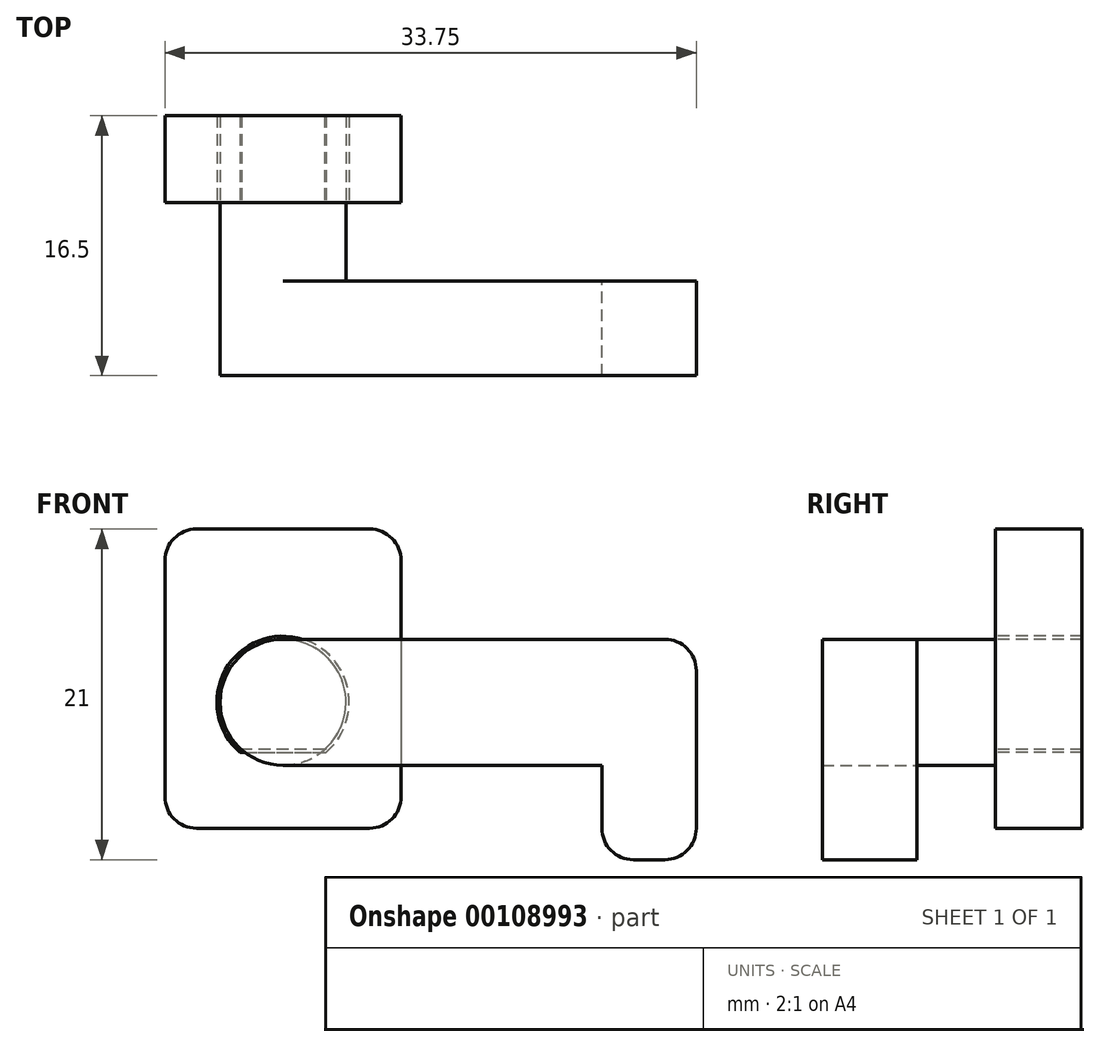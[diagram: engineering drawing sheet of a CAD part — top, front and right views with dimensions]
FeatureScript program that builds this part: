
annotation { "Feature Type Name" : "Feature", "Feature Type Description" : "" }
export const myFeature = defineFeature(function(context is Context, id is Id, definition is map)
    precondition{}
    {
        {
            var Q0;
            Q0=qCreatedBy(makeId("Front.planeOp"),FACE);
            var sketch = newSketch(context, id + "F0", { "sketchPlane" : qUnion([Q0])});
            skCircle(sketch, "E0", {"center": v(0, 0) * mm, "radius": 4 * mm});
            skLineSegment(sketch, "E1", {"start": v(-7.5, 11) * mm, "end": v(-7.5, -8) * mm});
            skLineSegment(sketch, "E2", {"start": v(-7.5, 11) * mm, "end": v(0, 11) * mm});
            skLineSegment(sketch, "E3", {"start": v(-7.5, -8) * mm, "end": v(0, -8) * mm});
            skLineSegment(sketch, "E4.MirrorCS", {"start": v(7.5, 11) * mm, "end": v(0, 11) * mm});
            skLineSegment(sketch, "E5.MirrorCS", {"start": v(7.5, 11) * mm, "end": v(7.5, -8) * mm});
            skLineSegment(sketch, "E6.MirrorCS", {"start": v(7.5, -8) * mm, "end": v(0, -8) * mm});
            skLineSegment(sketch, "E7", {"start": v(-7.5, -3) * mm, "end": v(7.5, -3) * mm});
            skCircle(sketch, "E8.0", {"center": v(0, 0) * mm, "radius": 4.2 * mm});
            skLineSegment(sketch, "E9.0", {"start": v(-7.5, -3.2) * mm, "end": v(7.5, -3.2) * mm});
            skSolve(sketch);
        }
        {
            var Q0;
            {var subQ1=sQuery(id+"F0.wireOp",EDGE,"E3");Q0=makeQuery(id+"F0.imprint","IMPRINT",FACE,{"disambiguationData":[TD([[makeQuery(id+"F0.imprint","IMPRINT",EDGE,{"derivedFrom":subQ1}),1.0]])]});}
            var Q1;
            {var subQ0=sQuery(id+"F0.wireOp",EDGE,"E9.0");var subQ1=sQuery(id+"F0.wireOp",EDGE,"E0");var subQ2=makeQuery(id+"F0.imprint","INTERSECT",VERTEX,{"disambiguationData":[OD(0.0)],"derivedFrom":[subQ1,subQ0]});Q1=makeQuery(id+"F0.imprint","IMPRINT",FACE,{"disambiguationData":[TD([[makeQuery(id+"F0.imprint","IMPRINT",EDGE,{"disambiguationData":[TD([[subQ2,-1.0]])],"derivedFrom":subQ1}),-1.0]])]});}
            var Q2;
            {var subQ0=sQuery(id+"F0.wireOp",EDGE,"E9.0");var subQ1=sQuery(id+"F0.wireOp",EDGE,"E0");var subQ2=makeQuery(id+"F0.imprint","INTERSECT",VERTEX,{"disambiguationData":[OD(0.0)],"derivedFrom":[subQ1,subQ0]});Q2=makeQuery(id+"F0.imprint","IMPRINT",FACE,{"disambiguationData":[TD([[makeQuery(id+"F0.imprint","IMPRINT",EDGE,{"disambiguationData":[TD([[subQ2,-1.0]])],"derivedFrom":subQ1}),1.0]])]});}
            var Q3;
            {var subQ0=sQuery(id+"F0.wireOp",EDGE,"E7");var subQ1=sQuery(id+"F0.wireOp",EDGE,"E5.MirrorCS");var subQ2=makeQuery(id+"F0.imprint","INTERSECT",VERTEX,{"derivedFrom":[subQ1,subQ0]});Q3=makeQuery(id+"F0.imprint","IMPRINT",FACE,{"disambiguationData":[TD([[makeQuery(id+"F0.imprint","IMPRINT",EDGE,{"disambiguationData":[TD([[subQ2,-1.0]])],"derivedFrom":subQ1}),-1.0]])]});}
            var Q4;
            {var subQ0=sQuery(id+"F0.wireOp",EDGE,"E7");var subQ1=sQuery(id+"F0.wireOp",EDGE,"E1");var subQ2=makeQuery(id+"F0.imprint","INTERSECT",VERTEX,{"derivedFrom":[subQ1,subQ0]});Q4=makeQuery(id+"F0.imprint","IMPRINT",FACE,{"disambiguationData":[TD([[makeQuery(id+"F0.imprint","IMPRINT",EDGE,{"disambiguationData":[TD([[subQ2,-1.0]])],"derivedFrom":subQ1}),1.0]])]});}
            var Q5;
            {var subQ7=sQuery(id+"F0.wireOp",EDGE,"E2");Q5=makeQuery(id+"F0.imprint","IMPRINT",FACE,{"disambiguationData":[TD([[makeQuery(id+"F0.imprint","IMPRINT",EDGE,{"derivedFrom":subQ7}),-1.0]])]});}
            extrude(context, id + "F1", {"entities" : qUnion([Q0, Q1, Q2, Q3, Q4, Q5]), "oppositeDirection" : true, "depth" : 5.5 * mm});
        }
        {
            var Q0;
            Q0=makeQuery(id+"F1.opExtrude","SWEPT_EDGE",EDGE,{"disambiguationData":[OSD([sQuery(id+"F0.wireOp",EDGE,"E1"),sQuery(id+"F0.wireOp",EDGE,"E3")])]});
            var Q1;
            Q1=makeQuery(id+"F1.opExtrude","SWEPT_EDGE",EDGE,{"disambiguationData":[OSD([sQuery(id+"F0.wireOp",EDGE,"E5.MirrorCS"),sQuery(id+"F0.wireOp",EDGE,"E6.MirrorCS")])]});
            var Q2;
            Q2=makeQuery(id+"F1.opExtrude","SWEPT_EDGE",EDGE,{"disambiguationData":[OSD([sQuery(id+"F0.wireOp",EDGE,"E1"),sQuery(id+"F0.wireOp",EDGE,"E2")])]});
            var Q3;
            Q3=makeQuery(id+"F1.opExtrude","SWEPT_EDGE",EDGE,{"disambiguationData":[OSD([sQuery(id+"F0.wireOp",EDGE,"E4.MirrorCS"),sQuery(id+"F0.wireOp",EDGE,"E5.MirrorCS")])]});
            fillet(context, id + "F2", {"entities" : qUnion([Q0, Q1, Q2, Q3]), "radius" : 2 * mm, "tangentPropagation" : true, "allowEdgeOverflow" : false});
        }
        {
            var Q0;
            {var subQ0=sQuery(id+"F0.wireOp",EDGE,"E7");var subQ1=sQuery(id+"F0.wireOp",EDGE,"E0");var subQ2=makeQuery(id+"F0.imprint","INTERSECT",VERTEX,{"disambiguationData":[OD(0.0)],"derivedFrom":[subQ1,subQ0]});Q0=makeQuery(id+"F0.imprint","IMPRINT",FACE,{"disambiguationData":[TD([[makeQuery(id+"F0.imprint","IMPRINT",EDGE,{"disambiguationData":[TD([[subQ2,1.0]])],"derivedFrom":subQ1}),1.0]])]});}
            var Q1;
            Q1=makeQuery(id+"F1.opExtrude","CAP_FACE",FACE,{"disambiguationData":[OSD([sQuery(id+"F0.wireOp",EDGE,"E0"),sQuery(id+"F0.wireOp",EDGE,"E1"),sQuery(id+"F0.wireOp",EDGE,"E2"),sQuery(id+"F0.wireOp",EDGE,"E3"),sQuery(id+"F0.wireOp",EDGE,"E4.MirrorCS"),sQuery(id+"F0.wireOp",EDGE,"E5.MirrorCS"),sQuery(id+"F0.wireOp",EDGE,"E6.MirrorCS")])],"isStart":false});
            extrude(context, id + "F3", {"entities" : qUnion([Q0]), "endBound" : BoundingType.UP_TO_SURFACE, "oppositeDirection" : true, "endBoundEntityFace" : qUnion([Q1]), "depth" : 25 * mm});
        }
        {
            var Q0;
            {var subQ0=sQuery(id+"F0.wireOp",EDGE,"E7");var subQ1=sQuery(id+"F0.wireOp",EDGE,"E0");var subQ2=makeQuery(id+"F0.imprint","INTERSECT",VERTEX,{"disambiguationData":[OD(0.0)],"derivedFrom":[subQ1,subQ0]});Q0=makeQuery(id+"F0.imprint","IMPRINT",FACE,{"disambiguationData":[TD([[makeQuery(id+"F0.imprint","IMPRINT",EDGE,{"disambiguationData":[TD([[subQ2,1.0]])],"derivedFrom":subQ1}),1.0]])]});}
            var Q1;
            {var subQ0=sQuery(id+"F0.wireOp",EDGE,"E9.0");var subQ1=sQuery(id+"F0.wireOp",EDGE,"E0");var subQ2=makeQuery(id+"F0.imprint","INTERSECT",VERTEX,{"disambiguationData":[OD(0.0)],"derivedFrom":[subQ1,subQ0]});Q1=makeQuery(id+"F0.imprint","IMPRINT",FACE,{"disambiguationData":[TD([[makeQuery(id+"F0.imprint","IMPRINT",EDGE,{"disambiguationData":[TD([[subQ2,1.0]])],"derivedFrom":subQ1}),1.0]])]});}
            var Q2;
            {var subQ0=sQuery(id+"F0.wireOp",EDGE,"E9.0");var subQ1=sQuery(id+"F0.wireOp",EDGE,"E0");var subQ2=makeQuery(id+"F0.imprint","INTERSECT",VERTEX,{"disambiguationData":[OD(0.0)],"derivedFrom":[subQ1,subQ0]});Q2=makeQuery(id+"F0.imprint","IMPRINT",FACE,{"disambiguationData":[TD([[makeQuery(id+"F0.imprint","IMPRINT",EDGE,{"disambiguationData":[TD([[subQ2,-1.0]])],"derivedFrom":subQ1}),1.0]])]});}
            extrude(context, id + "F4", {"entities" : qUnion([Q0, Q1, Q2]), "operationType" : NewBodyOperationType.ADD, "depth" : 5 * mm});
        }
        {
            var Q0;
            Q0=makeQuery(id+"F4.opExtrude","CAP_FACE",FACE,{"disambiguationData":[OSD([sQuery(id+"F0.wireOp",EDGE,"E0")])],"isStart":false});
            var sketch = newSketch(context, id + "F5", { "sketchPlane" : qUnion([Q0])});
            skLineSegment(sketch, "E10", {"start": v(0, 4) * mm, "end": v(18.25, 4) * mm});
            skLineSegment(sketch, "E11", {"start": v(0, -4) * mm, "end": v(18.25, -4) * mm});
            skArc(sketch, "E12", {"start": v(0, 4) * mm, "mid": v(-4, 0) * mm, "end": v(0, -4) * mm});
            skLineSegment(sketch, "E13", {"start": v(18.25, 10.29) * mm, "end": v(18.25, -14.12) * mm, "construction": true});
            skLineSegment(sketch, "E14", {"start": v(-5.71, -10) * mm, "end": v(30.22, -10) * mm, "construction": true});
            skLineSegment(sketch, "E15", {"start": v(20.25, 4) * mm, "end": v(26.25, 4) * mm});
            skLineSegment(sketch, "E16", {"start": v(26.25, 4) * mm, "end": v(26.25, -10) * mm});
            skLineSegment(sketch, "E17", {"start": v(26.25, -10) * mm, "end": v(20.25, -10) * mm});
            skLineSegment(sketch, "E18", {"start": v(20.25, -10) * mm, "end": v(20.25, -4) * mm});
            skLineSegment(sketch, "E19", {"start": v(20.25, -4) * mm, "end": v(18.25, -4) * mm});
            skLineSegment(sketch, "E20", {"start": v(20.25, 4) * mm, "end": v(18.25, 4) * mm});
            skSolve(sketch);
        }
        {
            var Q0;
            {var subQ1=sQuery(id+"F5.wireOp",EDGE,"E10");Q0=makeQuery(id+"F5.imprint","IMPRINT",FACE,{"disambiguationData":[TD([[makeQuery(id+"F5.imprint","IMPRINT",EDGE,{"derivedFrom":subQ1}),-1.0]])]});}
            var Q1;
            {var subQ0=sQuery(id+"F5.wireOp",EDGE,"E12");Q1=makeQuery(id+"F5.imprint","IMPRINT",FACE,{"disambiguationData":[TD([[makeQuery(id+"F5.imprint","IMPRINT",EDGE,{"derivedFrom":subQ0}),1.0]])]});}
            extrude(context, id + "F6", {"entities" : qUnion([Q0, Q1]), "operationType" : NewBodyOperationType.ADD, "depth" : 6 * mm});
        }
        {
            var Q0;
            Q0=makeQuery(id+"F6.opExtrude","SWEPT_EDGE",EDGE,{"disambiguationData":[OSD([sQuery(id+"F5.wireOp",EDGE,"E15"),sQuery(id+"F5.wireOp",EDGE,"E16")])]});
            var Q1;
            Q1=makeQuery(id+"F6.opExtrude","SWEPT_EDGE",EDGE,{"disambiguationData":[OSD([sQuery(id+"F5.wireOp",EDGE,"E16"),sQuery(id+"F5.wireOp",EDGE,"E17")])]});
            var Q2;
            Q2=makeQuery(id+"F6.opExtrude","SWEPT_EDGE",EDGE,{"disambiguationData":[OSD([sQuery(id+"F5.wireOp",EDGE,"E17"),sQuery(id+"F5.wireOp",EDGE,"E18")])]});
            fillet(context, id + "F7", {"entities" : qUnion([Q0, Q1, Q2]), "radius" : 2 * mm, "tangentPropagation" : true, "allowEdgeOverflow" : false});
        }
    });
